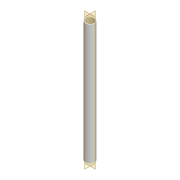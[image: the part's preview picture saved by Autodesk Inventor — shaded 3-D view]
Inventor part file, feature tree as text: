
AUTODESK INVENTOR PART (.ipt)
format: ipt  version: 2022 (Build 260153000, 153)  size: 77,824 bytes
history: native  units: mm
features: extrude x1, sketch x1
ambient origin geometry x8: Origin, YZ Plane, XZ Plane, XY Plane, X Axis, Y Axis, Z Axis, Center Point
bodies: Body1 (feature_tree)
feature tree (2):
  extrude  "Extrusion2"  Depth=150.0mm
  sketch  "Sketch2"  dims[d6=10.0mm d7=12.0mm d8=150.0mm d9=0.0mm]
